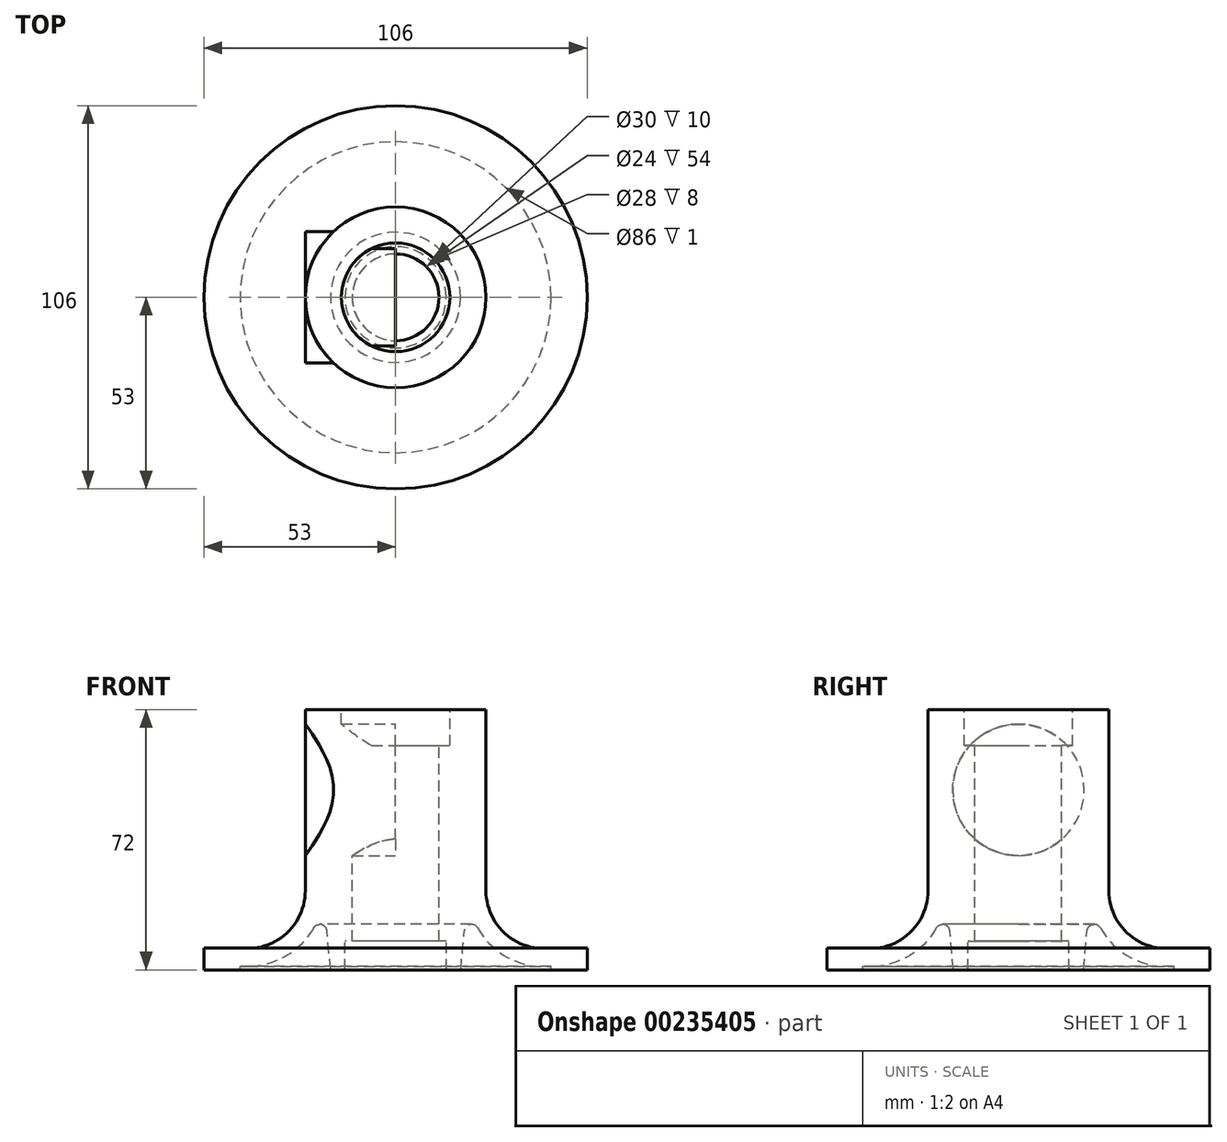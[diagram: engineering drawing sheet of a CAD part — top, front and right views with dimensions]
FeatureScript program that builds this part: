
annotation { "Feature Type Name" : "Feature", "Feature Type Description" : "" }
export const myFeature = defineFeature(function(context is Context, id is Id, definition is map)
    precondition{}
    {
        {
            var Q0;
            Q0=qCreatedBy(makeId("Front.planeOp"),FACE);
            var sketch = newSketch(context, id + "F0", { "sketchPlane" : qUnion([Q0])});
            skLineSegment(sketch, "E0", {"start": v(15, 72) * mm, "end": v(25, 72) * mm});
            skLineSegment(sketch, "E1", {"start": v(25, 72) * mm, "end": v(25, 21.9) * mm});
            skArc(sketch, "E2", {"start": v(25, 21.9) * mm, "mid": v(29.73, 10.55) * mm, "end": v(41.13, 5.9) * mm});
            skLineSegment(sketch, "E3", {"start": v(53, 6) * mm, "end": v(53, 0) * mm});
            skLineSegment(sketch, "E4", {"start": v(15, 72) * mm, "end": v(15, 62) * mm});
            skLineSegment(sketch, "E5", {"start": v(15, 62) * mm, "end": v(12, 62) * mm});
            skLineSegment(sketch, "E6", {"start": v(12, 62) * mm, "end": v(12, 8) * mm});
            skLineSegment(sketch, "E7", {"start": v(12, 8) * mm, "end": v(14, 8) * mm});
            skLineSegment(sketch, "E8", {"start": v(14, 8) * mm, "end": v(14, 0) * mm});
            skLineSegment(sketch, "E9", {"start": v(14, 0) * mm, "end": v(18, 0) * mm});
            skLineSegment(sketch, "E10", {"start": v(18, 0) * mm, "end": v(18.98, 10.77) * mm});
            skLineSegment(sketch, "E11", {"start": v(43, 0) * mm, "end": v(53, 0) * mm});
            skLineSegment(sketch, "E12", {"start": v(0, 74.4) * mm, "end": v(0, -10.88) * mm, "construction": true});
            skLineSegment(sketch, "E13", {"start": v(-29.02, 36) * mm, "end": v(43.04, 36) * mm, "construction": true});
            skLineSegment(sketch, "E14", {"start": v(43, 0) * mm, "end": v(43, 1) * mm});
            skArc(sketch, "E15.0", {"start": v(22.72, 11.57) * mm, "mid": v(31.3, 3.28) * mm, "end": v(43, 1) * mm});
            skLineSegment(sketch, "E16", {"start": v(41.13, 5.9) * mm, "end": v(53, 6) * mm});
            skPoint(sketch, "E17.visualSharp", {"position": v(20, 21.9) * mm});
            skArc(sketch, "E17.filletArc", {"start": v(22.72, 11.57) * mm, "mid": v(20.56, 12.55) * mm, "end": v(18.98, 10.77) * mm});
            skSolve(sketch);
        }
        {
            var Q0;
            Q0=makeQuery(id+"F0.imprint","IMPRINT",FACE,{"disambiguationData":[TD([[makeQuery(id+"F0.imprint","IMPRINT",EDGE,{"derivedFrom":sQuery(id+"F0.wireOp",EDGE,"E0")}),-1.0]])]});
            var Q1;
            Q1=sQuery(id+"F0.wireOp",EDGE,"E12");
            revolve(context, id + "F1", {"entities" : qUnion([Q0]), "axis" : qUnion([Q1]), "revolveType" : RevolveType.FULL});
        }
        {
            var Q0;
            Q0=qCreatedBy(makeId("Right.planeOp"),FACE);
            var sketch = newSketch(context, id + "F2", { "sketchPlane" : qUnion([Q0])});
            skLineSegment(sketch, "E18.0", {"start": v(-25, 72) * mm, "end": v(25, 72) * mm, "construction": true});
            skCircle(sketch, "E19", {"center": v(0, 49.78) * mm, "radius": 18.18 * mm});
            skSolve(sketch);
        }
        {
            var Q0;
            Q0 = qSketchRegion(id + "F2", true);
            extrude(context, id + "F3", {"entities" : qUnion([Q0]), "operationType" : NewBodyOperationType.ADD, "oppositeDirection" : true, "depth" : 25 * mm});
        }
    });
